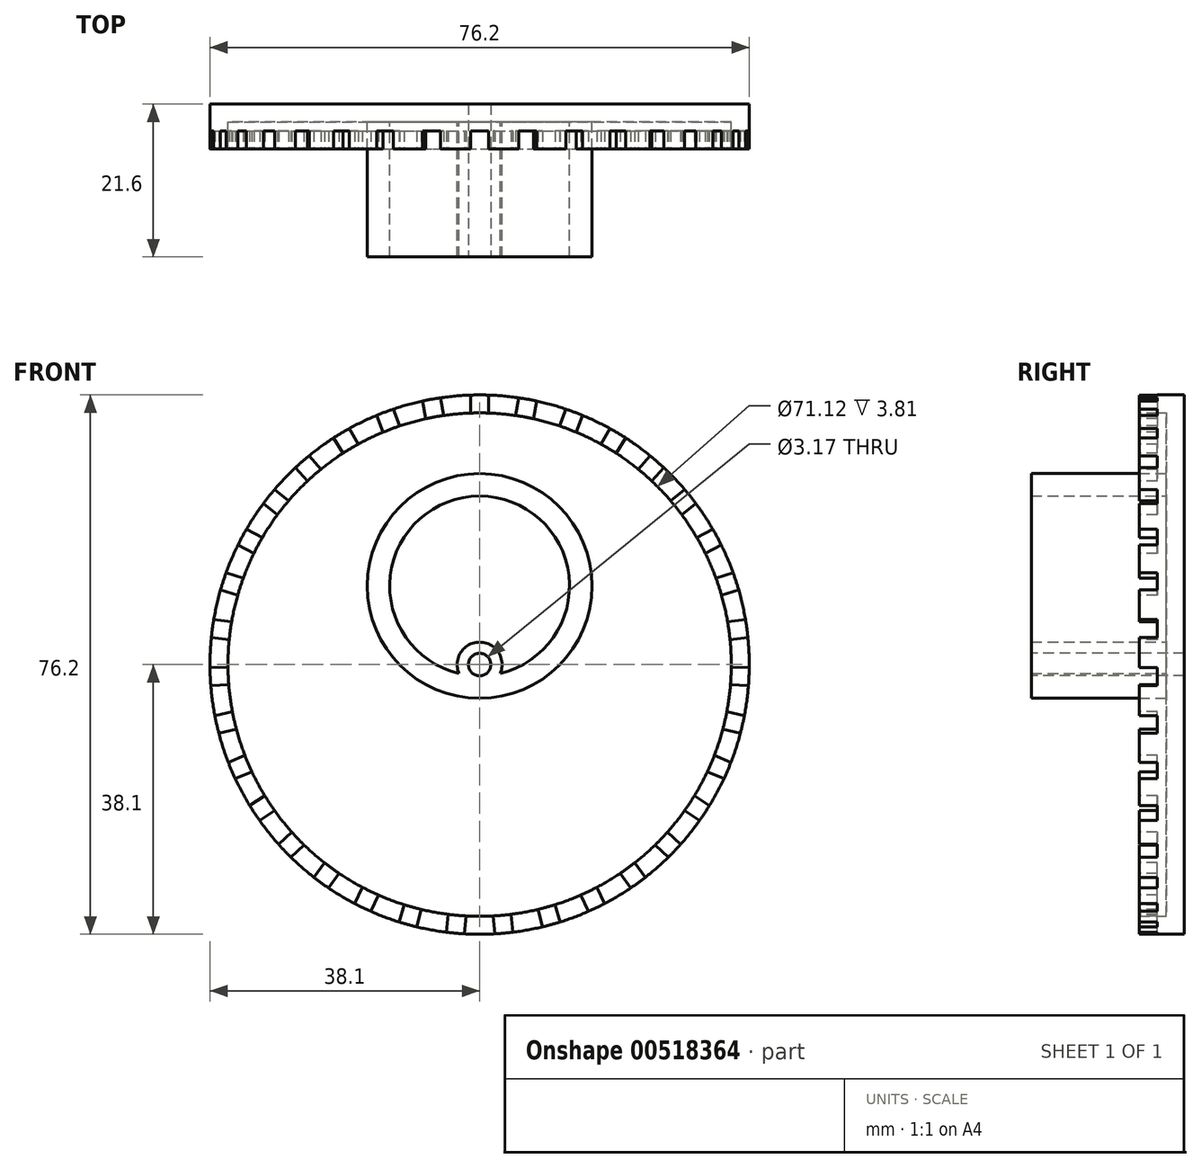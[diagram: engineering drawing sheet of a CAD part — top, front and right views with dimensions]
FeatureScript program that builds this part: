
annotation { "Feature Type Name" : "Feature", "Feature Type Description" : "" }
export const myFeature = defineFeature(function(context is Context, id is Id, definition is map)
    precondition{}
    {
        {
            var Q0;
            Q0=qCreatedBy(makeId("Front.planeOp"),FACE);
            var sketch = newSketch(context, id + "F0", { "sketchPlane" : qUnion([Q0])});
            skPoint(sketch, "E0.0", {"position": v(0, 0) * mm});
            skCircle(sketch, "E1", {"center": v(0, 0) * mm, "radius": 38.1 * mm});
            skSolve(sketch);
        }
        {
            var Q0;
            Q0 = qSketchRegion(id + "F0", true);
            extrude(context, id + "F1", {"entities" : qUnion([Q0]), "endBound" : BoundingType.SYMMETRIC, "depth" : 6.35 * mm, "offsetDistance" : 25.4 * mm});
        }
        {
            var Q0;
            Q0=makeQuery(id+"F1.opExtrude","CAP_FACE",FACE,{"disambiguationData":[OSD([sQuery(id+"F0.wireOp",EDGE,"E1")])],"isStart":false});
            shell(context, id + "F2", {"entities" : qUnion([Q0]), "thickness" : 2.54 * mm});
        }
        {
            var Q0;
            Q0=makeQuery(id+"F1.opExtrude","CAP_FACE",FACE,{"disambiguationData":[OSD([sQuery(id+"F0.wireOp",EDGE,"E1")])],"isStart":false});
            var sketch = newSketch(context, id + "F3", { "sketchPlane" : qUnion([Q0])});
            skArc(sketch, "E2", {"start": v(1.27, 38.08) * mm, "mid": v(0, 38.1) * mm, "end": v(-1.27, 38.08) * mm});
            skArc(sketch, "E3", {"start": v(1.27, 35.54) * mm, "mid": v(0, 35.56) * mm, "end": v(-1.27, 35.54) * mm});
            skLineSegment(sketch, "E4", {"start": v(-1.27, 38.08) * mm, "end": v(-1.27, 35.54) * mm});
            skLineSegment(sketch, "E5", {"start": v(0, 0) * mm, "end": v(0, 39.17) * mm, "construction": true});
            skLineSegment(sketch, "E6.MirrorCS", {"start": v(1.27, 38.08) * mm, "end": v(1.27, 35.54) * mm});
            skLineSegment(sketch, "E7.1.0", {"start": v(-5.55, 37.7) * mm, "end": v(-5.1, 35.2) * mm});
            skArc(sketch, "E7.1.1", {"start": v(-5.1, 35.2) * mm, "mid": v(-6.35, 34.99) * mm, "end": v(-7.6, 34.74) * mm});
            skLineSegment(sketch, "E7.1.2", {"start": v(-8.05, 37.24) * mm, "end": v(-7.6, 34.74) * mm});
            skArc(sketch, "E7.1.3", {"start": v(-5.55, 37.7) * mm, "mid": v(-6.8, 37.49) * mm, "end": v(-8.05, 37.24) * mm});
            skLineSegment(sketch, "E7.2.0", {"start": v(-12.2, 36.1) * mm, "end": v(-11.3, 33.72) * mm});
            skArc(sketch, "E7.2.1", {"start": v(-11.3, 33.72) * mm, "mid": v(-12.5, 33.3) * mm, "end": v(-13.68, 32.83) * mm});
            skLineSegment(sketch, "E7.2.2", {"start": v(-14.57, 35.2) * mm, "end": v(-13.68, 32.83) * mm});
            skArc(sketch, "E7.2.3", {"start": v(-12.2, 36.1) * mm, "mid": v(-13.39, 35.67) * mm, "end": v(-14.57, 35.2) * mm});
            skLineSegment(sketch, "E8.2.3.0", {"start": v(-18.44, 33.34) * mm, "end": v(-17.14, 31.16) * mm});
            skArc(sketch, "E8.3.3.0", {"start": v(-17.14, 31.16) * mm, "mid": v(-18.24, 30.53) * mm, "end": v(-19.32, 29.86) * mm});
            skLineSegment(sketch, "E8.7.3.0", {"start": v(-20.62, 32.04) * mm, "end": v(-19.32, 29.86) * mm});
            skArc(sketch, "E8.10.3.0", {"start": v(-18.44, 33.34) * mm, "mid": v(-19.54, 32.7) * mm, "end": v(-20.62, 32.04) * mm});
            skLineSegment(sketch, "E8.2.4.0", {"start": v(-24.1, 29.51) * mm, "end": v(-22.42, 27.6) * mm});
            skArc(sketch, "E8.3.4.0", {"start": v(-22.42, 27.6) * mm, "mid": v(-23.4, 26.78) * mm, "end": v(-24.34, 25.93) * mm});
            skLineSegment(sketch, "E8.7.4.0", {"start": v(-26, 27.84) * mm, "end": v(-24.34, 25.93) * mm});
            skArc(sketch, "E8.10.4.0", {"start": v(-24.1, 29.51) * mm, "mid": v(-25.07, 28.7) * mm, "end": v(-26, 27.84) * mm});
            skLineSegment(sketch, "E8.2.5.0", {"start": v(-28.98, 24.73) * mm, "end": v(-27, 23.15) * mm});
            skArc(sketch, "E8.3.5.0", {"start": v(-27, 23.15) * mm, "mid": v(-27.8, 22.17) * mm, "end": v(-28.58, 21.16) * mm});
            skLineSegment(sketch, "E8.7.5.0", {"start": v(-30.56, 22.75) * mm, "end": v(-28.58, 21.16) * mm});
            skArc(sketch, "E8.10.5.0", {"start": v(-28.98, 24.73) * mm, "mid": v(-29.79, 23.75) * mm, "end": v(-30.56, 22.75) * mm});
            skLineSegment(sketch, "E8.2.6.0", {"start": v(-32.93, 19.16) * mm, "end": v(-30.7, 17.96) * mm});
            skArc(sketch, "E8.3.6.0", {"start": v(-30.7, 17.96) * mm, "mid": v(-31.31, 16.85) * mm, "end": v(-31.9, 15.72) * mm});
            skLineSegment(sketch, "E8.7.6.0", {"start": v(-34.13, 16.93) * mm, "end": v(-31.9, 15.72) * mm});
            skArc(sketch, "E8.10.6.0", {"start": v(-32.93, 19.16) * mm, "mid": v(-33.55, 18.05) * mm, "end": v(-34.13, 16.93) * mm});
            skLineSegment(sketch, "E8.2.7.0", {"start": v(-35.82, 12.97) * mm, "end": v(-33.4, 12.19) * mm});
            skArc(sketch, "E8.3.7.0", {"start": v(-33.4, 12.19) * mm, "mid": v(-33.82, 10.99) * mm, "end": v(-34.2, 9.77) * mm});
            skLineSegment(sketch, "E8.7.7.0", {"start": v(-36.6, 10.56) * mm, "end": v(-34.2, 9.77) * mm});
            skArc(sketch, "E8.10.7.0", {"start": v(-35.82, 12.97) * mm, "mid": v(-36.24, 11.77) * mm, "end": v(-36.6, 10.56) * mm});
            skLineSegment(sketch, "E8.2.8.0", {"start": v(-37.56, 6.37) * mm, "end": v(-35.05, 6.03) * mm});
            skArc(sketch, "E8.3.8.0", {"start": v(-35.05, 6.03) * mm, "mid": v(-35.24, 4.77) * mm, "end": v(-35.39, 3.51) * mm});
            skLineSegment(sketch, "E8.7.8.0", {"start": v(-37.9, 3.85) * mm, "end": v(-35.39, 3.51) * mm});
            skArc(sketch, "E8.10.8.0", {"start": v(-37.56, 6.37) * mm, "mid": v(-37.76, 5.11) * mm, "end": v(-37.9, 3.85) * mm});
            skLineSegment(sketch, "E8.2.9.0", {"start": v(-38.1, -0.44) * mm, "end": v(-35.56, -0.33) * mm});
            skArc(sketch, "E8.3.9.0", {"start": v(-35.56, -0.33) * mm, "mid": v(-35.52, -1.6) * mm, "end": v(-35.44, -2.86) * mm});
            skLineSegment(sketch, "E8.7.9.0", {"start": v(-37.98, -2.98) * mm, "end": v(-35.44, -2.86) * mm});
            skArc(sketch, "E8.10.9.0", {"start": v(-38.1, -0.44) * mm, "mid": v(-38.06, -1.7) * mm, "end": v(-37.98, -2.98) * mm});
            skLineSegment(sketch, "E8.2.10.0", {"start": v(-37.4, -7.24) * mm, "end": v(-34.93, -6.67) * mm});
            skArc(sketch, "E8.3.10.0", {"start": v(-34.93, -6.67) * mm, "mid": v(-34.67, -7.91) * mm, "end": v(-34.36, -9.15) * mm});
            skLineSegment(sketch, "E8.7.10.0", {"start": v(-36.84, -9.71) * mm, "end": v(-34.36, -9.15) * mm});
            skArc(sketch, "E8.10.10.0", {"start": v(-37.4, -7.24) * mm, "mid": v(-37.14, -8.48) * mm, "end": v(-36.84, -9.71) * mm});
            skLineSegment(sketch, "E8.2.11.0", {"start": v(-35.51, -13.8) * mm, "end": v(-33.18, -12.8) * mm});
            skArc(sketch, "E8.3.11.0", {"start": v(-33.18, -12.8) * mm, "mid": v(-32.7, -13.98) * mm, "end": v(-32.18, -15.13) * mm});
            skLineSegment(sketch, "E8.7.11.0", {"start": v(-34.52, -16.13) * mm, "end": v(-32.18, -15.13) * mm});
            skArc(sketch, "E8.10.11.0", {"start": v(-35.51, -13.8) * mm, "mid": v(-35.03, -14.97) * mm, "end": v(-34.52, -16.13) * mm});
            skLineSegment(sketch, "E8.2.12.0", {"start": v(-32.48, -19.92) * mm, "end": v(-30.36, -18.52) * mm});
            skArc(sketch, "E8.3.12.0", {"start": v(-30.36, -18.52) * mm, "mid": v(-29.68, -19.59) * mm, "end": v(-28.96, -20.64) * mm});
            skLineSegment(sketch, "E8.7.12.0", {"start": v(-31.08, -22.04) * mm, "end": v(-28.96, -20.64) * mm});
            skArc(sketch, "E8.10.12.0", {"start": v(-32.48, -19.92) * mm, "mid": v(-31.8, -20.99) * mm, "end": v(-31.08, -22.04) * mm});
            skLineSegment(sketch, "E8.2.13.0", {"start": v(-28.4, -25.4) * mm, "end": v(-26.56, -23.64) * mm});
            skArc(sketch, "E8.3.13.0", {"start": v(-26.56, -23.64) * mm, "mid": v(-25.7, -24.57) * mm, "end": v(-24.8, -25.48) * mm});
            skLineSegment(sketch, "E8.7.13.0", {"start": v(-26.65, -27.23) * mm, "end": v(-24.8, -25.48) * mm});
            skArc(sketch, "E8.10.13.0", {"start": v(-28.4, -25.4) * mm, "mid": v(-27.54, -26.33) * mm, "end": v(-26.65, -27.23) * mm});
            skLineSegment(sketch, "E8.2.14.0", {"start": v(-23.4, -30.06) * mm, "end": v(-21.92, -28) * mm});
            skArc(sketch, "E8.3.14.0", {"start": v(-21.92, -28) * mm, "mid": v(-20.9, -28.77) * mm, "end": v(-19.86, -29.5) * mm});
            skLineSegment(sketch, "E8.7.14.0", {"start": v(-21.35, -31.55) * mm, "end": v(-19.86, -29.5) * mm});
            skArc(sketch, "E8.10.14.0", {"start": v(-23.4, -30.06) * mm, "mid": v(-22.4, -30.82) * mm, "end": v(-21.35, -31.55) * mm});
            skLineSegment(sketch, "E8.2.15.0", {"start": v(-17.67, -33.76) * mm, "end": v(-16.56, -31.47) * mm});
            skArc(sketch, "E8.3.15.0", {"start": v(-16.56, -31.47) * mm, "mid": v(-15.43, -32.04) * mm, "end": v(-14.27, -32.57) * mm});
            skLineSegment(sketch, "E8.7.15.0", {"start": v(-15.38, -34.86) * mm, "end": v(-14.27, -32.57) * mm});
            skArc(sketch, "E8.10.15.0", {"start": v(-17.67, -33.76) * mm, "mid": v(-16.53, -34.33) * mm, "end": v(-15.38, -34.86) * mm});
            skLineSegment(sketch, "E8.2.16.0", {"start": v(-11.35, -36.37) * mm, "end": v(-10.68, -33.92) * mm});
            skArc(sketch, "E8.3.16.0", {"start": v(-10.68, -33.92) * mm, "mid": v(-9.46, -34.28) * mm, "end": v(-8.23, -34.6) * mm});
            skLineSegment(sketch, "E8.7.16.0", {"start": v(-8.9, -37.04) * mm, "end": v(-8.23, -34.6) * mm});
            skArc(sketch, "E8.10.16.0", {"start": v(-11.35, -36.37) * mm, "mid": v(-10.14, -36.73) * mm, "end": v(-8.9, -37.04) * mm});
            skLineSegment(sketch, "E8.2.17.0", {"start": v(-4.68, -37.81) * mm, "end": v(-4.45, -35.28) * mm});
            skArc(sketch, "E8.3.17.0", {"start": v(-4.45, -35.28) * mm, "mid": v(-3.19, -35.42) * mm, "end": v(-1.92, -35.5) * mm});
            skLineSegment(sketch, "E8.7.17.0", {"start": v(-2.15, -38.04) * mm, "end": v(-1.92, -35.5) * mm});
            skArc(sketch, "E8.10.17.0", {"start": v(-4.68, -37.81) * mm, "mid": v(-3.42, -37.95) * mm, "end": v(-2.15, -38.04) * mm});
            skLineSegment(sketch, "E8.2.18.0", {"start": v(2.15, -38.04) * mm, "end": v(1.92, -35.5) * mm});
            skArc(sketch, "E8.3.18.0", {"start": v(1.92, -35.5) * mm, "mid": v(3.19, -35.42) * mm, "end": v(4.45, -35.28) * mm});
            skLineSegment(sketch, "E8.7.18.0", {"start": v(4.68, -37.81) * mm, "end": v(4.45, -35.28) * mm});
            skArc(sketch, "E8.10.18.0", {"start": v(2.15, -38.04) * mm, "mid": v(3.42, -37.95) * mm, "end": v(4.68, -37.81) * mm});
            skLineSegment(sketch, "E8.2.19.0", {"start": v(8.9, -37.04) * mm, "end": v(8.23, -34.6) * mm});
            skArc(sketch, "E8.3.19.0", {"start": v(8.23, -34.6) * mm, "mid": v(9.46, -34.28) * mm, "end": v(10.68, -33.92) * mm});
            skLineSegment(sketch, "E8.7.19.0", {"start": v(11.35, -36.37) * mm, "end": v(10.68, -33.92) * mm});
            skArc(sketch, "E8.10.19.0", {"start": v(8.9, -37.04) * mm, "mid": v(10.14, -36.73) * mm, "end": v(11.35, -36.37) * mm});
            skLineSegment(sketch, "E9.2.20.0", {"start": v(15.38, -34.86) * mm, "end": v(14.27, -32.57) * mm});
            skArc(sketch, "E9.3.20.0", {"start": v(14.27, -32.57) * mm, "mid": v(15.43, -32.04) * mm, "end": v(16.56, -31.47) * mm});
            skLineSegment(sketch, "E9.7.20.0", {"start": v(17.67, -33.76) * mm, "end": v(16.56, -31.47) * mm});
            skArc(sketch, "E9.10.20.0", {"start": v(15.38, -34.86) * mm, "mid": v(16.53, -34.33) * mm, "end": v(17.67, -33.76) * mm});
            skLineSegment(sketch, "E9.2.21.0", {"start": v(21.35, -31.55) * mm, "end": v(19.86, -29.5) * mm});
            skArc(sketch, "E9.3.21.0", {"start": v(19.86, -29.5) * mm, "mid": v(20.9, -28.77) * mm, "end": v(21.92, -28) * mm});
            skLineSegment(sketch, "E9.7.21.0", {"start": v(23.4, -30.06) * mm, "end": v(21.92, -28) * mm});
            skArc(sketch, "E9.10.21.0", {"start": v(21.35, -31.55) * mm, "mid": v(22.4, -30.82) * mm, "end": v(23.4, -30.06) * mm});
            skLineSegment(sketch, "E9.2.22.0", {"start": v(26.65, -27.23) * mm, "end": v(24.8, -25.48) * mm});
            skArc(sketch, "E9.3.22.0", {"start": v(24.8, -25.48) * mm, "mid": v(25.7, -24.57) * mm, "end": v(26.56, -23.64) * mm});
            skLineSegment(sketch, "E9.7.22.0", {"start": v(28.4, -25.4) * mm, "end": v(26.56, -23.64) * mm});
            skArc(sketch, "E9.10.22.0", {"start": v(26.65, -27.23) * mm, "mid": v(27.54, -26.33) * mm, "end": v(28.4, -25.4) * mm});
            skLineSegment(sketch, "E9.2.23.0", {"start": v(31.08, -22.04) * mm, "end": v(28.96, -20.64) * mm});
            skArc(sketch, "E9.3.23.0", {"start": v(28.96, -20.64) * mm, "mid": v(29.68, -19.59) * mm, "end": v(30.36, -18.52) * mm});
            skLineSegment(sketch, "E9.7.23.0", {"start": v(32.48, -19.92) * mm, "end": v(30.36, -18.52) * mm});
            skArc(sketch, "E9.10.23.0", {"start": v(31.08, -22.04) * mm, "mid": v(31.8, -20.99) * mm, "end": v(32.48, -19.92) * mm});
            skLineSegment(sketch, "E9.2.24.0", {"start": v(34.52, -16.13) * mm, "end": v(32.18, -15.13) * mm});
            skArc(sketch, "E9.3.24.0", {"start": v(32.18, -15.13) * mm, "mid": v(32.7, -13.98) * mm, "end": v(33.18, -12.8) * mm});
            skLineSegment(sketch, "E9.7.24.0", {"start": v(35.51, -13.8) * mm, "end": v(33.18, -12.8) * mm});
            skArc(sketch, "E9.10.24.0", {"start": v(34.52, -16.13) * mm, "mid": v(35.03, -14.97) * mm, "end": v(35.51, -13.8) * mm});
            skLineSegment(sketch, "E10.2.25.0", {"start": v(36.84, -9.71) * mm, "end": v(34.36, -9.15) * mm});
            skArc(sketch, "E10.3.25.0", {"start": v(34.36, -9.15) * mm, "mid": v(34.67, -7.91) * mm, "end": v(34.93, -6.67) * mm});
            skLineSegment(sketch, "E10.7.25.0", {"start": v(37.4, -7.24) * mm, "end": v(34.93, -6.67) * mm});
            skArc(sketch, "E10.10.25.0", {"start": v(36.84, -9.71) * mm, "mid": v(37.14, -8.48) * mm, "end": v(37.4, -7.24) * mm});
            skLineSegment(sketch, "E10.2.26.0", {"start": v(37.98, -2.98) * mm, "end": v(35.44, -2.86) * mm});
            skArc(sketch, "E10.3.26.0", {"start": v(35.44, -2.86) * mm, "mid": v(35.52, -1.6) * mm, "end": v(35.56, -0.33) * mm});
            skLineSegment(sketch, "E10.7.26.0", {"start": v(38.1, -0.44) * mm, "end": v(35.56, -0.33) * mm});
            skArc(sketch, "E10.10.26.0", {"start": v(37.98, -2.98) * mm, "mid": v(38.06, -1.7) * mm, "end": v(38.1, -0.44) * mm});
            skLineSegment(sketch, "E10.2.27.0", {"start": v(37.9, 3.85) * mm, "end": v(35.39, 3.51) * mm});
            skArc(sketch, "E10.3.27.0", {"start": v(35.39, 3.51) * mm, "mid": v(35.24, 4.77) * mm, "end": v(35.05, 6.03) * mm});
            skLineSegment(sketch, "E10.7.27.0", {"start": v(37.56, 6.37) * mm, "end": v(35.05, 6.03) * mm});
            skArc(sketch, "E10.10.27.0", {"start": v(37.9, 3.85) * mm, "mid": v(37.76, 5.11) * mm, "end": v(37.56, 6.37) * mm});
            skLineSegment(sketch, "E10.2.28.0", {"start": v(36.6, 10.56) * mm, "end": v(34.2, 9.77) * mm});
            skArc(sketch, "E10.3.28.0", {"start": v(34.2, 9.77) * mm, "mid": v(33.82, 10.99) * mm, "end": v(33.4, 12.19) * mm});
            skLineSegment(sketch, "E10.7.28.0", {"start": v(35.82, 12.97) * mm, "end": v(33.4, 12.19) * mm});
            skArc(sketch, "E10.10.28.0", {"start": v(36.6, 10.56) * mm, "mid": v(36.24, 11.77) * mm, "end": v(35.82, 12.97) * mm});
            skLineSegment(sketch, "E10.2.29.0", {"start": v(34.13, 16.93) * mm, "end": v(31.9, 15.72) * mm});
            skArc(sketch, "E10.3.29.0", {"start": v(31.9, 15.72) * mm, "mid": v(31.31, 16.85) * mm, "end": v(30.7, 17.96) * mm});
            skLineSegment(sketch, "E10.7.29.0", {"start": v(32.93, 19.16) * mm, "end": v(30.7, 17.96) * mm});
            skArc(sketch, "E10.10.29.0", {"start": v(34.13, 16.93) * mm, "mid": v(33.55, 18.05) * mm, "end": v(32.93, 19.16) * mm});
            skLineSegment(sketch, "E11.2.30.0", {"start": v(30.56, 22.75) * mm, "end": v(28.58, 21.16) * mm});
            skArc(sketch, "E11.3.30.0", {"start": v(28.58, 21.16) * mm, "mid": v(27.8, 22.17) * mm, "end": v(27, 23.15) * mm});
            skLineSegment(sketch, "E11.7.30.0", {"start": v(28.98, 24.73) * mm, "end": v(27, 23.15) * mm});
            skArc(sketch, "E11.10.30.0", {"start": v(30.56, 22.75) * mm, "mid": v(29.79, 23.75) * mm, "end": v(28.98, 24.73) * mm});
            skLineSegment(sketch, "E11.2.31.0", {"start": v(26, 27.84) * mm, "end": v(24.34, 25.93) * mm});
            skArc(sketch, "E11.3.31.0", {"start": v(24.34, 25.93) * mm, "mid": v(23.4, 26.78) * mm, "end": v(22.42, 27.6) * mm});
            skLineSegment(sketch, "E11.7.31.0", {"start": v(24.1, 29.51) * mm, "end": v(22.42, 27.6) * mm});
            skArc(sketch, "E11.10.31.0", {"start": v(26, 27.84) * mm, "mid": v(25.07, 28.7) * mm, "end": v(24.1, 29.51) * mm});
            skLineSegment(sketch, "E11.2.32.0", {"start": v(20.62, 32.04) * mm, "end": v(19.32, 29.86) * mm});
            skArc(sketch, "E11.3.32.0", {"start": v(19.32, 29.86) * mm, "mid": v(18.24, 30.53) * mm, "end": v(17.14, 31.16) * mm});
            skLineSegment(sketch, "E11.7.32.0", {"start": v(18.44, 33.34) * mm, "end": v(17.14, 31.16) * mm});
            skArc(sketch, "E11.10.32.0", {"start": v(20.62, 32.04) * mm, "mid": v(19.54, 32.7) * mm, "end": v(18.44, 33.34) * mm});
            skLineSegment(sketch, "E11.2.33.0", {"start": v(14.57, 35.2) * mm, "end": v(13.68, 32.83) * mm});
            skArc(sketch, "E11.3.33.0", {"start": v(13.68, 32.83) * mm, "mid": v(12.5, 33.3) * mm, "end": v(11.3, 33.72) * mm});
            skLineSegment(sketch, "E11.7.33.0", {"start": v(12.2, 36.1) * mm, "end": v(11.3, 33.72) * mm});
            skArc(sketch, "E11.10.33.0", {"start": v(14.57, 35.2) * mm, "mid": v(13.39, 35.67) * mm, "end": v(12.2, 36.1) * mm});
            skLineSegment(sketch, "E11.2.34.0", {"start": v(8.05, 37.24) * mm, "end": v(7.6, 34.74) * mm});
            skArc(sketch, "E11.3.34.0", {"start": v(7.6, 34.74) * mm, "mid": v(6.35, 34.99) * mm, "end": v(5.1, 35.2) * mm});
            skLineSegment(sketch, "E11.7.34.0", {"start": v(5.55, 37.7) * mm, "end": v(5.1, 35.2) * mm});
            skArc(sketch, "E11.10.34.0", {"start": v(8.05, 37.24) * mm, "mid": v(6.8, 37.49) * mm, "end": v(5.55, 37.7) * mm});
            skSolve(sketch);
        }
        {
            var Q0;
            Q0 = qSketchRegion(id + "F3", true);
            extrude(context, id + "F4", {"entities" : qUnion([Q0]), "operationType" : NewBodyOperationType.REMOVE, "oppositeDirection" : true, "depth" : 2.54 * mm, "offsetDistance" : 25.4 * mm});
        }
        {
            var Q0;
            {var subQ0=sQuery(id+"F0.wireOp",EDGE,"E1");Q0=makeQuery(id+"F2.opShell","OFFSET_FACE",FACE,{"disambiguationData":[OSD([subQ0]),TDD([makeQuery(id+"F1.opExtrude","CAP_FACE",FACE,{"disambiguationData":[OSD([subQ0])],"isStart":true})])]});}
            var sketch = newSketch(context, id + "F5", { "sketchPlane" : qUnion([Q0])});
            skCircle(sketch, "E12", {"center": v(0, 0) * mm, "radius": 1.59 * mm});
            skSolve(sketch);
        }
        {
            var Q0;
            Q0 = qSketchRegion(id + "F5", true);
            extrude(context, id + "F6", {"entities" : qUnion([Q0]), "operationType" : NewBodyOperationType.REMOVE, "oppositeDirection" : true, "depth" : 25.4 * mm, "offsetDistance" : 25.4 * mm});
        }
        {
            var Q0;
            {var subQ0=sQuery(id+"F0.wireOp",EDGE,"E1");Q0=makeQuery(id+"F2.opShell","OFFSET_FACE",FACE,{"disambiguationData":[OSD([subQ0]),TDD([makeQuery(id+"F1.opExtrude","CAP_FACE",FACE,{"disambiguationData":[OSD([subQ0])],"isStart":true})])]});}
            var sketch = newSketch(context, id + "F7", { "sketchPlane" : qUnion([Q0])});
            skCircle(sketch, "E13", {"center": v(0, 0) * mm, "radius": 3.18 * mm});
            skCircle(sketch, "E14", {"center": v(0, 0) * mm, "radius": 1.59 * mm});
            skSolve(sketch);
        }
        {
            var Q0;
            Q0 = qSketchRegion(id + "F7", true);
            extrude(context, id + "F8", {"entities" : qUnion([Q0]), "operationType" : NewBodyOperationType.ADD, "depth" : 19.05 * mm, "offsetDistance" : 25.4 * mm});
        }
        {
            var Q0;
            {var subQ0=sQuery(id+"F0.wireOp",EDGE,"E1");Q0=makeQuery(id+"F2.opShell","OFFSET_FACE",FACE,{"disambiguationData":[OSD([subQ0]),TDD([makeQuery(id+"F1.opExtrude","CAP_FACE",FACE,{"disambiguationData":[OSD([subQ0])],"isStart":true})])]});}
            var sketch = newSketch(context, id + "F9", { "sketchPlane" : qUnion([Q0])});
            skCircle(sketch, "E15", {"center": v(0, 11.11) * mm, "radius": 12.7 * mm});
            skCircle(sketch, "E16", {"center": v(0, 11.11) * mm, "radius": 15.88 * mm});
            skSolve(sketch);
        }
        {
            var Q0;
            Q0 = qSketchRegion(id + "F9", true);
            extrude(context, id + "F10", {"entities" : qUnion([Q0]), "operationType" : NewBodyOperationType.ADD, "depth" : 19.05 * mm, "offsetDistance" : 25.4 * mm});
        }
    });
